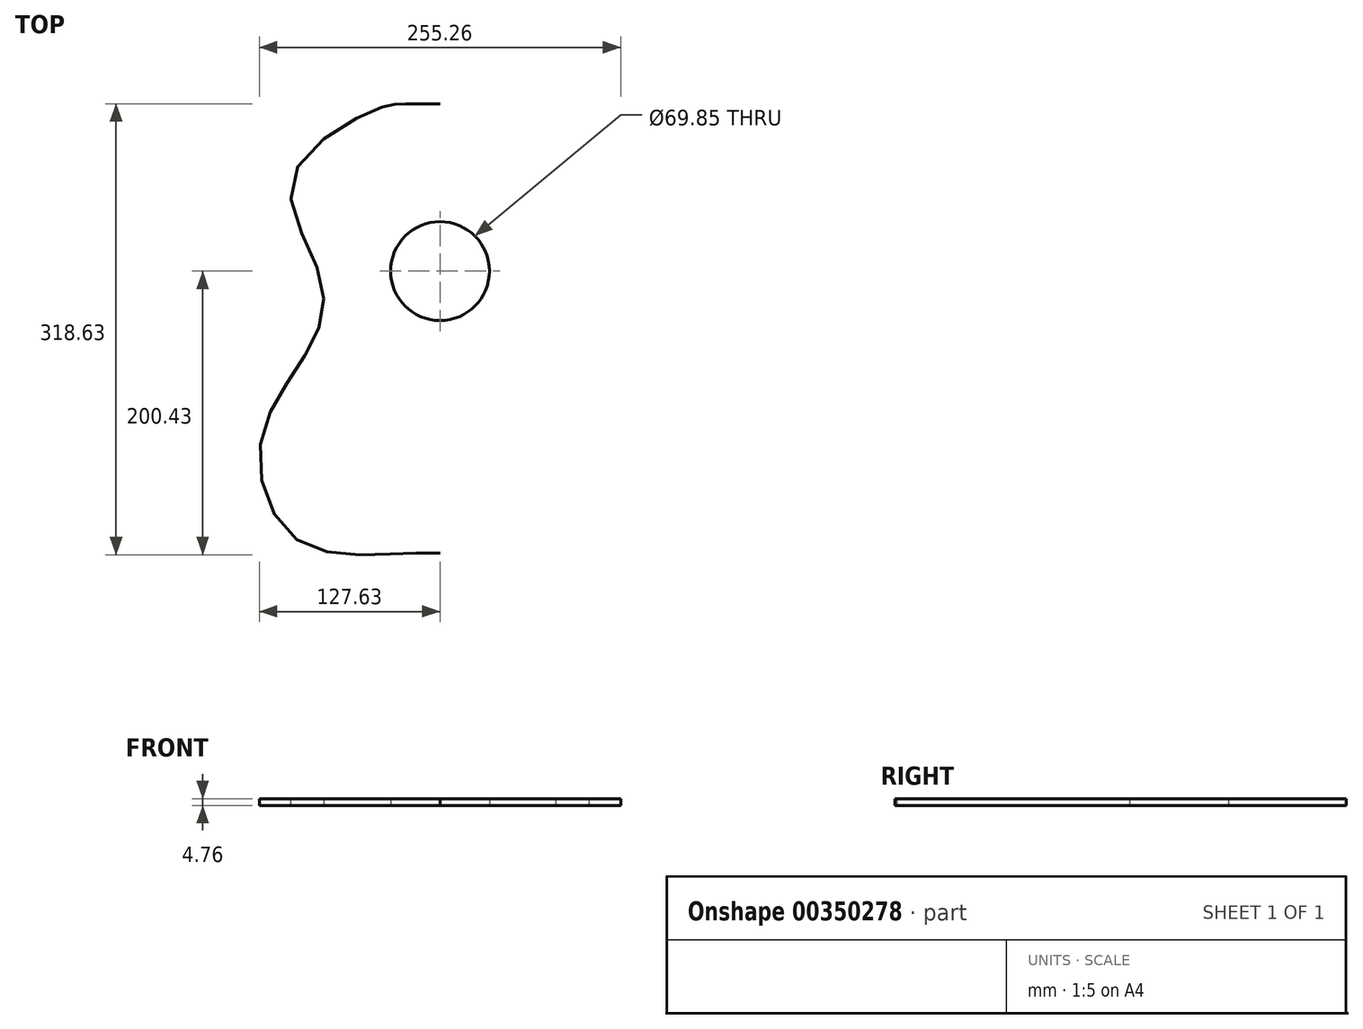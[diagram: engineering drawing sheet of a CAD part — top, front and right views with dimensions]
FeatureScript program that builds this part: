
annotation { "Feature Type Name" : "Feature", "Feature Type Description" : "" }
export const myFeature = defineFeature(function(context is Context, id is Id, definition is map)
    precondition{}
    {
        {
            var Q0;
            Q0=qCreatedBy(makeId("Top.planeOp"),FACE);
            var sketch = newSketch(context, id + "F0", { "sketchPlane" : qUnion([Q0])});
            skFitSpline(sketch, "E0", {"points": [v(0, 118.1) * mm, v(-32.12, 117.82) * mm, v(-44.9, 114.6) * mm, v(-104.3, 65.36) * mm, v(-83.5, -7.95) * mm, v(-96.22, -60.94) * mm, v(-127, -122.47) * mm, v(-101.73, -189.4) * mm, v(-39.45, -200) * mm, v(0, -199.4) * mm], "startDerivative": vector(-904.68, 6.6) * mm, "endDerivative": vector(409.06, -6.1) * mm});
            skLineSegment(sketch, "E1", {"start": v(0, 216.78) * mm, "end": v(0, -225.2) * mm});
            skFitSpline(sketch, "E2.MirrorCS", {"points": [v(0, 118.1) * mm, v(32.12, 117.82) * mm, v(44.9, 114.6) * mm, v(104.3, 65.36) * mm, v(83.5, -7.95) * mm, v(96.22, -60.94) * mm, v(127, -122.47) * mm, v(101.73, -189.4) * mm, v(39.45, -200) * mm, v(0, -199.4) * mm], "startDerivative": vector(904.68, 6.6) * mm, "endDerivative": vector(-409.06, -6.1) * mm});
            skCircle(sketch, "E3", {"center": v(0, 0) * mm, "radius": 34.93 * mm});
            skSolve(sketch);
        }
        {
            var Q0;
            {var subQ0=sQuery(id+"F0.wireOp",EDGE,"E0");Q0=makeQuery(id+"F0.imprint","IMPRINT",FACE,{"disambiguationData":[TD([[makeQuery(id+"F0.imprint","IMPRINT",EDGE,{"derivedFrom":subQ0}),1.0]])]});}
            var Q1;
            {var subQ0=sQuery(id+"F0.wireOp",EDGE,"E2.MirrorCS");Q1=makeQuery(id+"F0.imprint","IMPRINT",FACE,{"disambiguationData":[TD([[makeQuery(id+"F0.imprint","IMPRINT",EDGE,{"derivedFrom":subQ0}),-1.0]])]});}
            extrude(context, id + "F1", {"entities" : qUnion([Q0, Q1]), "depth" : 4.76 * mm});
        }
    });
